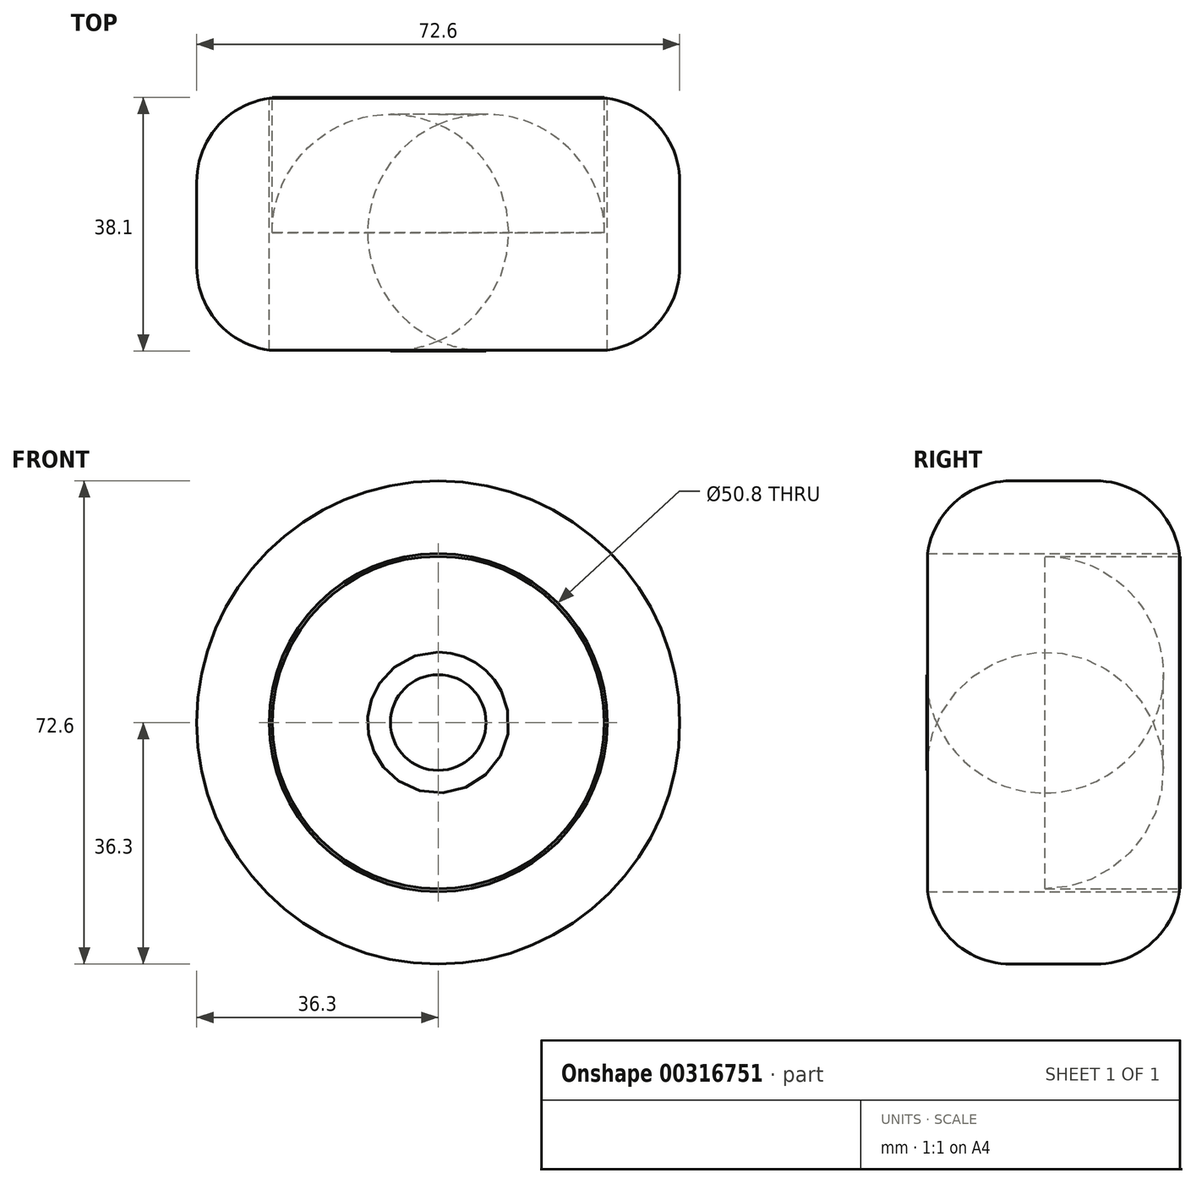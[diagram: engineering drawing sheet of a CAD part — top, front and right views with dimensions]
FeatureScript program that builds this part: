
annotation { "Feature Type Name" : "Feature", "Feature Type Description" : "" }
export const myFeature = defineFeature(function(context is Context, id is Id, definition is map)
    precondition{}
    {
        {
            var Q0;
            Q0=qCreatedBy(makeId("Front.planeOp"),FACE);
            var sketch = newSketch(context, id + "F0", { "sketchPlane" : qUnion([Q0])});
            skCircle(sketch, "E0", {"center": v(0, 0) * mm, "radius": 36.3 * mm});
            skSolve(sketch);
        }
        {
            var Q0;
            Q0 = qSketchRegion(id + "F0", true);
            extrude(context, id + "F1", {"entities" : qUnion([Q0]), "depth" : 38.1 * mm});
        }
        {
            var Q0;
            Q0=makeQuery(id+"F1.opExtrude","CAP_EDGE",EDGE,{"disambiguationData":[OSD([sQuery(id+"F0.wireOp",EDGE,"E0")])],"isStart":false});
            var Q1;
            Q1=makeQuery(id+"F1.opExtrude","CAP_EDGE",EDGE,{"disambiguationData":[OSD([sQuery(id+"F0.wireOp",EDGE,"E0")])],"isStart":true});
            fillet(context, id + "F2", {"entities" : qUnion([Q0, Q1]), "radius" : 12.7 * mm, "tangentPropagation" : true, "allowEdgeOverflow" : false});
        }
        {
            var Q0;
            Q0=sQuery(id+"F0.wireOp",VERTEX,"E0.center");
            var Q1;
            Q1=makeQuery(id+"F1.opExtrude","SWEPT_BODY",BODY,{"disambiguationData":[OSD([sQuery(id+"F0.wireOp",EDGE,"E0")])]});
            hole(context, id + "F3", {"style" : HoleStyle.SIMPLE, "endStyle" : HoleEndStyle.BLIND, "oppositeDirection" : true, "holeDiameter" : 50.8 * mm, "holeDepth" : 76.2 * mm, "tappedDepth" : 12.7 * mm, "tapClearance" : 3, "locations" : qUnion([Q0]), "scope" : qUnion([Q1])});
        }
        {
            var Q0;
            Q0=makeQuery(id+"F0.imprint","IMPRINT",FACE,{"disambiguationData":[TD([[makeQuery(id+"F0.imprint","IMPRINT",EDGE,{"derivedFrom":sQuery(id+"F0.wireOp",EDGE,"E0")}),1.0]])]});
            var sketch = newSketch(context, id + "F4", { "sketchPlane" : qUnion([Q0])});
            skCircle(sketch, "E1", {"center": v(0, 0) * mm, "radius": 24.97 * mm});
            skSolve(sketch);
        }
        {
            var Q0;
            Q0 = qSketchRegion(id + "F4", true);
            extrude(context, id + "F5", {"entities" : qUnion([Q0]), "depth" : 38.1 * mm});
        }
        {
            var Q0;
            Q0=makeQuery(id+"F5.opExtrude","CAP_FACE",FACE,{"disambiguationData":[OSD([sQuery(id+"F4.wireOp",EDGE,"E1")])],"isStart":false});
            fillet(context, id + "F6", {"entities" : qUnion([Q0]), "radius" : 17.78 * mm, "tangentPropagation" : true, "allowEdgeOverflow" : false});
        }
    });
